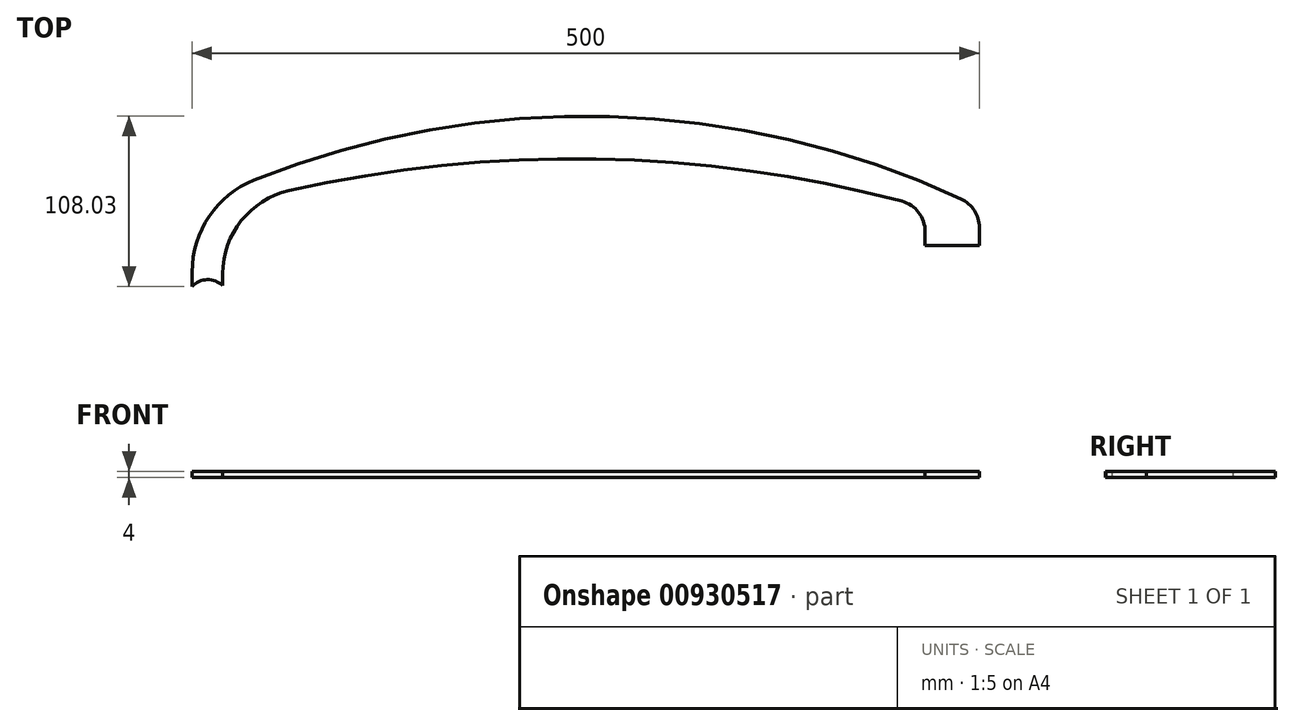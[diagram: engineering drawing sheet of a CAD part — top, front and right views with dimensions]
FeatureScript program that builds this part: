
annotation { "Feature Type Name" : "Feature", "Feature Type Description" : "" }
export const myFeature = defineFeature(function(context is Context, id is Id, definition is map)
    precondition{}
    {
        {
            var Q0;
            Q0=qCreatedBy(makeId("Top.planeOp"),FACE);
            var sketch = newSketch(context, id + "F0", { "sketchPlane" : qUnion([Q0])});
            skArc(sketch, "E0", {"start": v(231.7, 0) * mm, "mid": v(8.61, 31) * mm, "end": v(-214.47, 0) * mm});
            skArc(sketch, "E1", {"start": v(266.08, 0) * mm, "mid": v(16.08, 58.03) * mm, "end": v(-233.92, 0) * mm});
            skLineSegment(sketch, "E2", {"start": v(-233.92, 0) * mm, "end": v(-233.92, -50) * mm});
            skLineSegment(sketch, "E3", {"start": v(-214.47, 0) * mm, "end": v(-214.47, -49.46) * mm});
            skArc(sketch, "E4", {"start": v(-214.47, -49.46) * mm, "mid": v(-224.3, -45.77) * mm, "end": v(-233.92, -50) * mm});
            skLineSegment(sketch, "E5", {"start": v(231.7, 0) * mm, "end": v(231.7, -24.02) * mm});
            skLineSegment(sketch, "E6", {"start": v(231.7, -24.02) * mm, "end": v(266.08, -24.02) * mm});
            skLineSegment(sketch, "E7", {"start": v(266.08, -24.02) * mm, "end": v(266.08, 0) * mm});
            skSolve(sketch);
        }
        {
            var Q0;
            Q0 = qSketchRegion(id + "F0", true);
            extrude(context, id + "F1", {"entities" : qUnion([Q0]), "depth" : 4 * mm, "offsetDistance" : 25 * mm});
        }
        {
            var Q0;
            {var subQ0=sQuery(id+"F0.wireOp",EDGE,"E3");var subQ1=sQuery(id+"F0.wireOp",EDGE,"E0");Q0=makeQuery(id+"FNQGh9nQSZqUYQv_0.boolean.opBoolean","MERGE",EDGE,{"derivedFrom":[makeQuery(id+"F1.opExtrude","SWEPT_EDGE",EDGE,{"disambiguationData":[OSD([subQ1,subQ0])]}),makeQuery(id+"FNQGh9nQSZqUYQv_0.opExtrude","SWEPT_EDGE",EDGE,{"disambiguationData":[OSD([subQ1,subQ0])]})]});}
            fillet(context, id + "F2", {"entities" : qUnion([Q0]), "radius" : 54.02 * mm, "tangentPropagation" : true, "allowEdgeOverflow" : false});
        }
        {
            var Q0;
            {var subQ0=sQuery(id+"F0.wireOp",EDGE,"E2");var subQ1=sQuery(id+"F0.wireOp",EDGE,"E1");Q0=makeQuery(id+"FNQGh9nQSZqUYQv_0.boolean.opBoolean","MERGE",EDGE,{"derivedFrom":[makeQuery(id+"F1.opExtrude","SWEPT_EDGE",EDGE,{"disambiguationData":[OSD([subQ1,subQ0])]}),makeQuery(id+"FNQGh9nQSZqUYQv_0.opExtrude","SWEPT_EDGE",EDGE,{"disambiguationData":[OSD([subQ1,subQ0])]})]});}
            fillet(context, id + "F3", {"entities" : qUnion([Q0]), "radius" : 62.8 * mm, "tangentPropagation" : true, "allowEdgeOverflow" : false});
        }
        {
            var Q0;
            Q0=makeQuery(id+"F1.opExtrude","CAP_FACE",FACE,{"disambiguationData":[OSD([sQuery(id+"F0.wireOp",EDGE,"E0"),sQuery(id+"F0.wireOp",EDGE,"E1"),sQuery(id+"F0.wireOp",EDGE,"l27CePmu-HyMm-vpyd-UL48-yFk1Gte5bMYs"),sQuery(id+"F0.wireOp",EDGE,"E2"),sQuery(id+"F0.wireOp",EDGE,"E3"),sQuery(id+"F0.wireOp",EDGE,"E4")])],"isStart":false});
            var sketch = newSketch(context, id + "F4", { "sketchPlane" : qUnion([Q0])});
            skLineSegment(sketch, "E8", {"start": v(231.7, 0) * mm, "end": v(231.7, -20.34) * mm});
            skLineSegment(sketch, "E9", {"start": v(231.7, -20.34) * mm, "end": v(266.08, -20.34) * mm});
            skLineSegment(sketch, "E10", {"start": v(266.08, -20.34) * mm, "end": v(266.08, 0) * mm});
            skLineSegment(sketch, "E11", {"start": v(231.7, 0) * mm, "end": v(266.08, 0) * mm});
            skSolve(sketch);
        }
        {
            var Q0;
            Q0 = qSketchRegion(id + "F4", true);
            extrude(context, id + "F5", {"entities" : qUnion([Q0]), "depth" : 4 * mm, "offsetDistance" : 25 * mm});
        }
        {
            var Q0;
            Q0=makeQuery(id+"F5.opExtrude","SWEPT_BODY",BODY,{"disambiguationData":[OSD([sQuery(id+"F4.wireOp",EDGE,"E8"),sQuery(id+"F4.wireOp",EDGE,"E9"),sQuery(id+"F4.wireOp",EDGE,"E10"),sQuery(id+"F4.wireOp",EDGE,"E11")])]});
            deleteBodies(context, id + "F6", {"entities" : qUnion([Q0])});
        }
        {
            var Q0;
            Q0=makeQuery(id+"F1.opExtrude","SWEPT_EDGE",EDGE,{"disambiguationData":[OSD([sQuery(id+"F0.wireOp",EDGE,"E1"),sQuery(id+"F0.wireOp",EDGE,"E7")])]});
            var Q1;
            Q1=makeQuery(id+"F1.opExtrude","SWEPT_EDGE",EDGE,{"disambiguationData":[OSD([sQuery(id+"F0.wireOp",EDGE,"E0"),sQuery(id+"F0.wireOp",EDGE,"E5")])]});
            fillet(context, id + "F7", {"entities" : qUnion([Q0, Q1]), "radius" : 20 * mm, "tangentPropagation" : true, "allowEdgeOverflow" : false});
        }
    });
